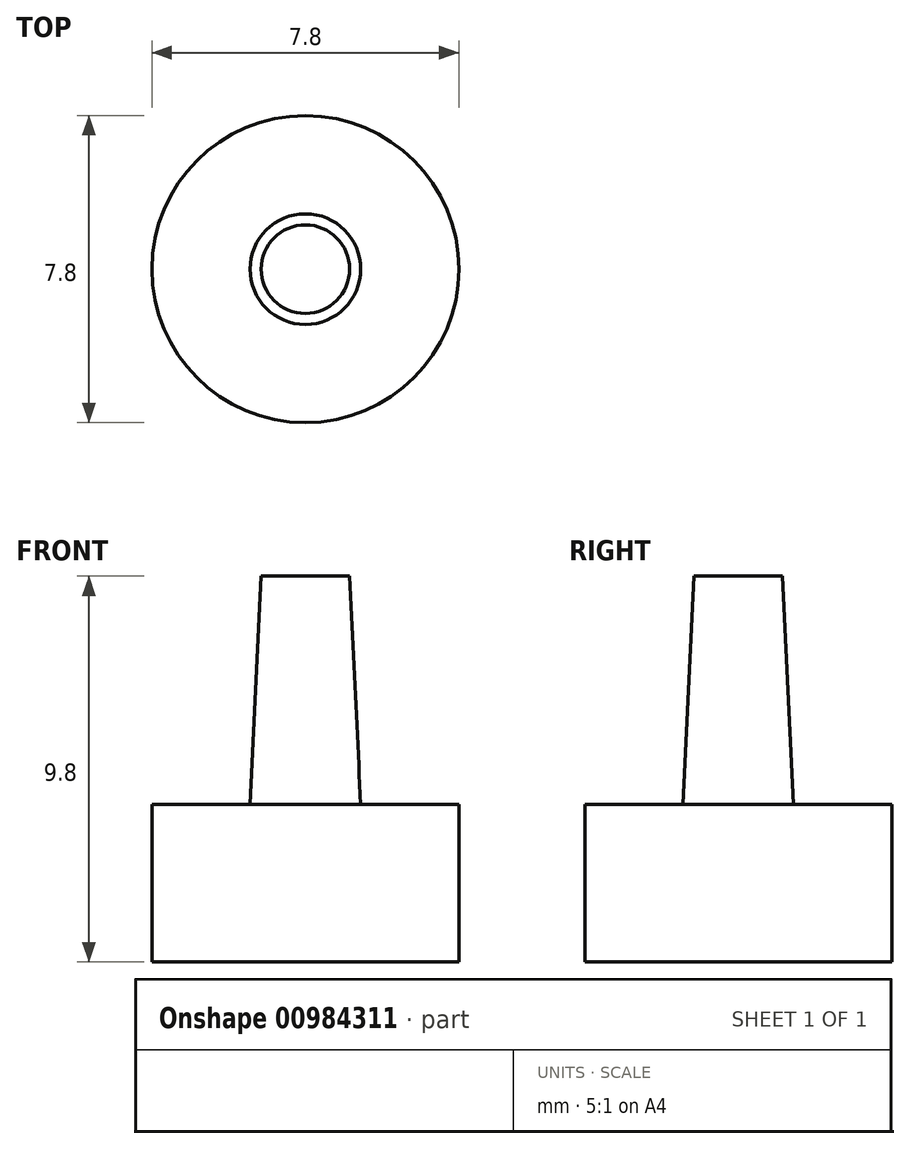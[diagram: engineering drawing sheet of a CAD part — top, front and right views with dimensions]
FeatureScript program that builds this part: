
annotation { "Feature Type Name" : "Feature", "Feature Type Description" : "" }
export const myFeature = defineFeature(function(context is Context, id is Id, definition is map)
    precondition{}
    {
        {
            var Q0;
            Q0=qCreatedBy(makeId("Top.planeOp"),FACE);
            var sketch = newSketch(context, id + "F0", { "sketchPlane" : qUnion([Q0])});
            skCircle(sketch, "E0", {"center": v(0, 0) * mm, "radius": 3.9 * mm});
            skSolve(sketch);
        }
        {
            var Q0;
            Q0 = qSketchRegion(id + "F0", true);
            extrude(context, id + "F1", {"entities" : qUnion([Q0]), "oppositeDirection" : true, "depth" : 4 * mm, "offsetDistance" : 25 * mm});
        }
        {
            var Q0;
            Q0=qCreatedBy(makeId("Top.planeOp"),FACE);
            var sketch = newSketch(context, id + "F2", { "sketchPlane" : qUnion([Q0])});
            skCircle(sketch, "E1", {"center": v(0, 0) * mm, "radius": 1.4 * mm});
            skSolve(sketch);
        }
        {
            var Q0;
            Q0=qCreatedBy(makeId("Top.planeOp"),FACE);
            cPlane(context, id + "F3", {"entities" : qUnion([Q0]), "cplaneType" : CPlaneType.OFFSET, "offset" : 5.8 * mm, "width" : 150 * mm, "height" : 150 * mm});
        }
        {
            var Q0;
            Q0=qCreatedBy(id+"F3.planeOp",FACE);
            var sketch = newSketch(context, id + "F4", { "sketchPlane" : qUnion([Q0])});
            skCircle(sketch, "E2", {"center": v(0, 0) * mm, "radius": 1.13 * mm});
            skSolve(sketch);
        }
        {
            var Q1;
            Q1 = qSketchRegion(id + "F2", true);
            var Q2;
            Q2 = qSketchRegion(id + "F4", true);
            loft(context, id + "F5", {"operationType" : NewBodyOperationType.ADD, "sheetProfilesArray" : [{ "sheetProfileEntities" : qUnion([Q1]) }, { "sheetProfileEntities" : qUnion([Q2]) }]});
        }
    });
